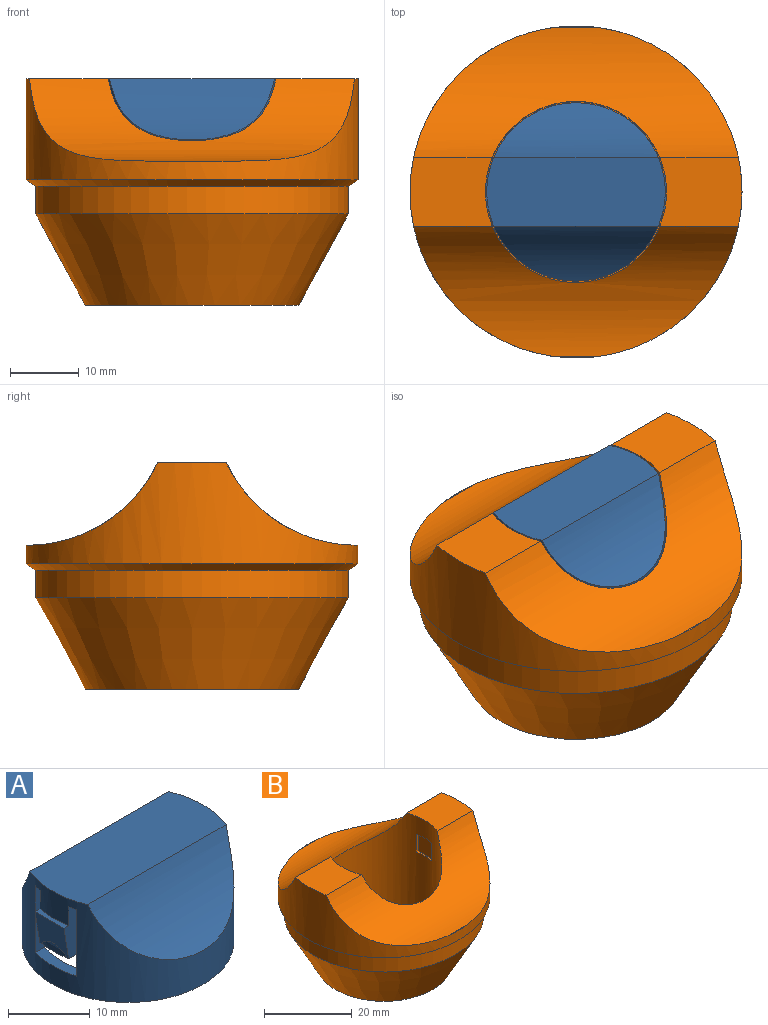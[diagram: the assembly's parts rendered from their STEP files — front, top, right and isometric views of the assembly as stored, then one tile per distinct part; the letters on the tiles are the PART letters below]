
ASSEMBLY  parts=2 mates=1
PART A: 33 faces, bbox 27.2x26x14 mm
  f0: plane 10x1.57mm, normal (0,1,0), area 15.7mm2, adj f13,f21,f22,f27
  f1: plane 10x1.57mm, normal (0,-1,0), area 15.7mm2, adj f7,f10,f13,f27
  f2: plane 7.8x2.38mm, normal (0,1,0), area 14.2mm2, adj f6,f7,f13,f19,f25,f28
  f3: plane 7.8x2.38mm, normal (0,1,0), area 14.2mm2, adj f13,f17,f18,f20,f26,f29
  f4: plane 7.8x2.38mm, normal (0,-1,0), area 14.2mm2, adj f6,f8,f13,f19,f25,f28
  f5: plane 7.8x2.38mm, normal (0,-1,0), area 14.2mm2, adj f13,f17,f18,f22,f26,f29
  f6: plane 5x1.78mm, normal (0,0,-1), area 7.6mm2, adj f2,f4,f15,f25,f28
  f7: plane 1.82x1.06mm, normal (0,0,-1), area 1.6mm2, adj f1,f2,f13,f28
  f8: plane 1.82x1.05mm, normal (0,0,-1), area 1.6mm2, adj f4,f11,f13,f28
  f9: plane 10x1.57mm, normal (0,-1,0), area 15.7mm2, adj f13,f20,f21,f27
  f10: plane 7.11x2.07mm, normal (0,0,1), area 10.8mm2, adj f1,f11,f13,f27
  f11: plane 10x1.57mm, normal (0,1,0), area 15.7mm2, adj f8,f10,f13,f27
  f12: plane 26x10mm, normal (0,0,1), area 253.4mm2, adj f13,f23,f24
  f13: cylinder r=13mm len=26mm, axis (0,0,-1), area 631.6mm2, adj f0,f1,f2,f3,f4,f5,f7,f8
  f14: cylinder r=13mm len=4.54mm, axis (0,0,-1), area 3.8mm2, adj f18,f26
  f15: cylinder r=13mm len=4.54mm, axis (0,0,-1), area 3.8mm2, adj f6,f25
  f16: plane 26x26mm, normal (0,0,-1), area 115.5mm2, adj f13,f27
  f17: plane 5x0.84mm, normal (0,0,1), area 3.4mm2, adj f3,f5,f13,f26
  f18: plane 5x1.78mm, normal (0,0,-1), area 7.6mm2, adj f3,f5,f14,f26,f29
  f19: plane 5x0.84mm, normal (0,0,1), area 3.4mm2, adj f2,f4,f13,f25
  f20: plane 1.82x1.06mm, normal (0,0,-1), area 1.6mm2, adj f3,f9,f13,f29
  f21: plane 7.11x2.07mm, normal (0,0,1), area 10.8mm2, adj f0,f9,f13,f27
  f22: plane 1.82x1.05mm, normal (0,0,-1), area 1.6mm2, adj f0,f5,f13,f29
  f23: cylinder r=21mm len=24mm, axis (1,0,0), area 221.5mm2, adj f12,f13
  f24: cylinder r=21mm len=24mm, axis (1,0,0), area 221.4mm2, adj f12,f13
  f25: plane 5x5mm, normal (-0.99,0,-0.16), area 21.5mm2, adj f2,f4,f6,f15,f19
  f26: plane 5x5mm, normal (0.99,0,-0.16), area 21.5mm2, adj f3,f5,f14,f17,f18
  f27: cylinder r=11.5mm len=23mm, axis (0,0,-1), area 494.3mm2, adj f0,f1,f9,f10,f11,f16,f21,f28
  f28: cylinder r=11.5mm len=8mm, axis (0,0,-1), area 40.8mm2, adj f2,f4,f6,f7,f8,f27,f30
  f29: cylinder r=11.5mm len=8mm, axis (0,0,-1), area 40.8mm2, adj f3,f5,f18,f20,f22,f27,f30
  f30: plane 23x7.11mm, normal (0,0,-1), area 160.9mm2, adj f28,f29,f31,f32
  f31: plane 21.87x7.94mm, normal (0,-0.71,-0.71), area 179.7mm2, adj f27,f30
  f32: plane 21.88x7.95mm, normal (0,0.71,-0.71), area 180.3mm2, adj f27,f30
PART B: 27 faces, bbox 48.4x48.4x33 mm
  f0: cylinder r=13.2mm len=30.2mm, axis (0,0,1), area 2044mm2, adj f1,f2,f3,f12,f14,f15,f16,f18
  f1: plane 11.98x10mm, normal (0,0,1), area 111.5mm2, adj f0,f4,f24,f25
  f2: plane 26.4x26.4mm, normal (0,0,1), area 411.2mm2, adj f0,f8,f9,f10,f11
  f3: plane 11.98x10mm, normal (0,0,1), area 111.5mm2, adj f0,f4,f24,f25
  f4: cylinder r=24.2mm len=48.4mm, axis (0,0,1), area 947.7mm2, adj f1,f3,f22,f23,f24,f25,f26
  f5: cylinder r=22.8mm len=45.6mm, axis (0,0,1), area 575.4mm2, adj f6,f26
  f6: cone r=15.58mm half-angle=28.5deg, axis (0,0,1), area 1824.7mm2, adj f5,f7
  f7: plane 31.15x31.15mm, normal (0,0,-1), area 625.9mm2, adj f6,f8,f9,f10,f11
  f8: cylinder r=7mm len=11mm, axis (0,0,-1), area 35.4mm2, adj f2,f7,f9,f10
  f9: plane 8.66x2.8mm, normal (1,0,0), area 24.2mm2, adj f2,f7,f8,f11
  f10: plane 8.66x2.8mm, normal (-1,0,0), area 24.2mm2, adj f2,f7,f8,f11
  f11: cylinder r=7mm len=11mm, axis (0,0,-1), area 35.4mm2, adj f2,f7,f9,f10
  f12: plane 5x0.64mm, normal (0,-1,0), area 3.2mm2, adj f0,f13,f15,f16
  f13: plane 5x5mm, normal (1,0,0), area 25mm2, adj f12,f14,f15,f16
  f14: plane 5x0.64mm, normal (0,1,0), area 3.2mm2, adj f0,f13,f15,f16
  f15: plane 5x0.64mm, normal (0,0,1), area 2.4mm2, adj f0,f12,f13,f14
  f16: plane 5x0.64mm, normal (0,0,-1), area 2.4mm2, adj f0,f12,f13,f14
  f17: plane 5x5mm, normal (-1,0,0), area 25mm2, adj f18,f19,f20,f21
  f18: plane 5x0.64mm, normal (0,-1,0), area 3.2mm2, adj f0,f17,f20,f21
  f19: plane 5x0.64mm, normal (0,1,0), area 3.2mm2, adj f0,f17,f20,f21
  f20: plane 5x0.64mm, normal (0,0,1), area 2.4mm2, adj f0,f17,f18,f19
  f21: plane 5x0.64mm, normal (0,0,-1), area 2.4mm2, adj f0,f17,f18,f19
  f22: plane 6.6x0.23mm, normal (0,0,1), area 1mm2, adj f4,f24
  f23: plane 6.6x0.23mm, normal (0,0,1), area 1mm2, adj f4,f25
  f24: cylinder r=21mm len=47.36mm, axis (1,0,0), area 658.4mm2, adj f0,f1,f3,f4,f22
  f25: cylinder r=21mm len=47.36mm, axis (-1,0,0), area 658.4mm2, adj f0,f1,f3,f4,f23
  f26: cone r=24.2mm half-angle=56.3deg, axis (0,0,1), area 248.4mm2, adj f4,f5
PLACE A t=(59.39,0,19)mm
PLACE B at identity
MATE fastened A.f13 <-> B.f0  axis (0,0,1) through (0,0,33)mm
